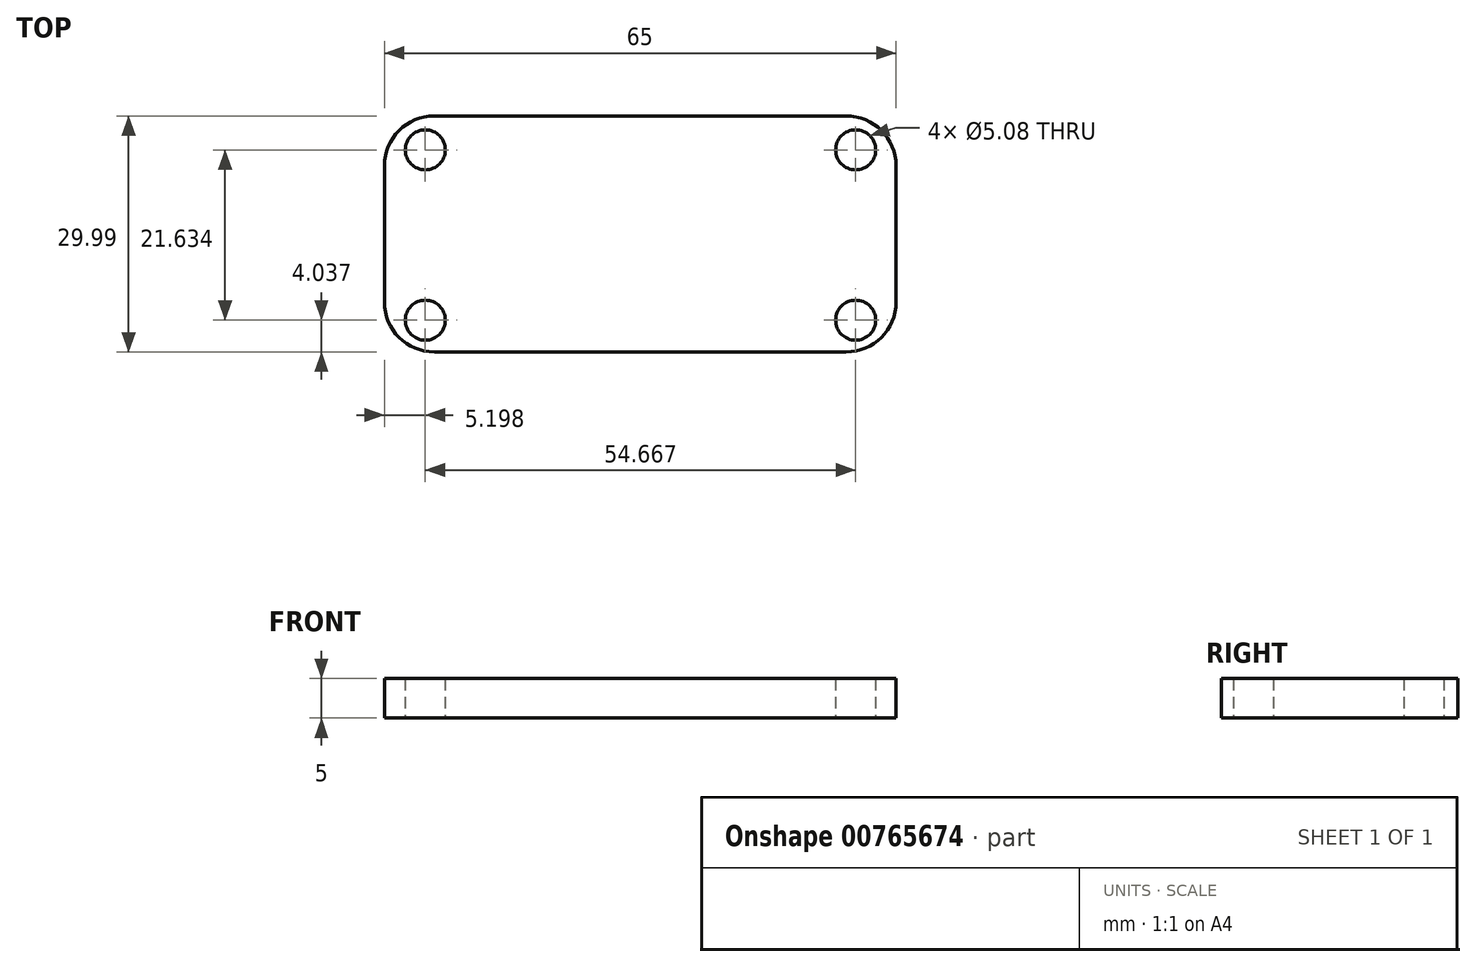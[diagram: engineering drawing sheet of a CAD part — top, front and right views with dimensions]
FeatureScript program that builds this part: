
annotation { "Feature Type Name" : "Feature", "Feature Type Description" : "" }
export const myFeature = defineFeature(function(context is Context, id is Id, definition is map)
    precondition{}
    {
        {
            var Q0;
            Q0=qCreatedBy(makeId("Top.planeOp"),FACE);
            var sketch = newSketch(context, id + "F0", { "sketchPlane" : qUnion([Q0])});
            skLineSegment(sketch, "E0.bottom", {"start": v(-27.3, 15.2) * mm, "end": v(25, 15.2) * mm});
            skLineSegment(sketch, "E0.top", {"start": v(-27.3, -14.8) * mm, "end": v(25, -14.8) * mm});
            skLineSegment(sketch, "E0.left", {"start": v(-33.65, 8.85) * mm, "end": v(-33.65, -8.44) * mm});
            skLineSegment(sketch, "E0.right", {"start": v(31.35, 8.85) * mm, "end": v(31.35, -8.44) * mm});
            skPoint(sketch, "E1.visualSharp", {"position": v(-33.65, 15.2) * mm});
            skArc(sketch, "E1.filletArc", {"start": v(-27.3, 15.2) * mm, "mid": v(-31.8, 13.35) * mm, "end": v(-33.65, 8.85) * mm});
            skPoint(sketch, "E2.visualSharp", {"position": v(-33.65, -14.8) * mm});
            skArc(sketch, "E2.filletArc", {"start": v(-33.65, -8.44) * mm, "mid": v(-31.8, -12.94) * mm, "end": v(-27.3, -14.8) * mm});
            skPoint(sketch, "E3.visualSharp", {"position": v(31.35, 15.2) * mm});
            skArc(sketch, "E3.filletArc", {"start": v(31.35, 8.85) * mm, "mid": v(29.49, 13.35) * mm, "end": v(25, 15.2) * mm});
            skPoint(sketch, "E4.visualSharp", {"position": v(31.35, -14.8) * mm});
            skArc(sketch, "E4.filletArc", {"start": v(25, -14.8) * mm, "mid": v(29.49, -12.94) * mm, "end": v(31.35, -8.44) * mm});
            skSolve(sketch);
        }
        {
            var Q0;
            Q0=makeQuery(id+"F0.imprint","IMPRINT",FACE,{"disambiguationData":[TD([[makeQuery(id+"F0.imprint","IMPRINT",EDGE,{"derivedFrom":sQuery(id+"F0.wireOp",EDGE,"E0.bottom")}),-1.0]])]});
            extrude(context, id + "F1", {"entities" : qUnion([Q0]), "depth" : 5 * mm, "offsetDistance" : 25.4 * mm});
        }
        {
            var Q0;
            Q0=qCreatedBy(makeId("Top.planeOp"),FACE);
            var sketch = newSketch(context, id + "F2", { "sketchPlane" : qUnion([Q0])});
            skCircle(sketch, "E5", {"center": v(-28.45, 10.88) * mm, "radius": 2.54 * mm});
            skCircle(sketch, "E6", {"center": v(-28.45, -10.75) * mm, "radius": 2.54 * mm});
            skCircle(sketch, "E7", {"center": v(26.22, -10.75) * mm, "radius": 2.54 * mm});
            skCircle(sketch, "E8", {"center": v(26.22, 10.88) * mm, "radius": 2.54 * mm});
            skSolve(sketch);
        }
        {
            var Q0;
            Q0 = qSketchRegion(id + "F2", true);
            extrude(context, id + "F3", {"entities" : qUnion([Q0]), "operationType" : NewBodyOperationType.REMOVE, "endBound" : BoundingType.SYMMETRIC, "depth" : 25.4 * mm, "offsetDistance" : 25.4 * mm});
        }
        {
            var Q0;
            Q0=qCreatedBy(makeId("Right.planeOp"),FACE);
            var sketch = newSketch(context, id + "F4", { "sketchPlane" : qUnion([Q0])});
            skLineSegment(sketch, "E9.bottom", {"start": v(6.93, 3.07) * mm, "end": v(-4.07, 3.07) * mm});
            skLineSegment(sketch, "E9.top", {"start": v(6.93, 2.07) * mm, "end": v(-4.07, 2.07) * mm});
            skLineSegment(sketch, "E9.left", {"start": v(6.93, 3.07) * mm, "end": v(6.93, 2.07) * mm});
            skLineSegment(sketch, "E9.right", {"start": v(-4.07, 3.07) * mm, "end": v(-4.07, 2.07) * mm});
            skSolve(sketch);
        }
        {
            var Q0;
            Q0=sQuery(id+"F4.wireOp",EDGE,"E9.top");
            extrude(context, id + "F5", {"bodyType" : ToolBodyType.SURFACE, "surfaceEntities" : qUnion([Q0]), "oppositeDirection" : true, "depth" : 38.1 * mm, "offsetDistance" : 25.4 * mm});
        }
    });
